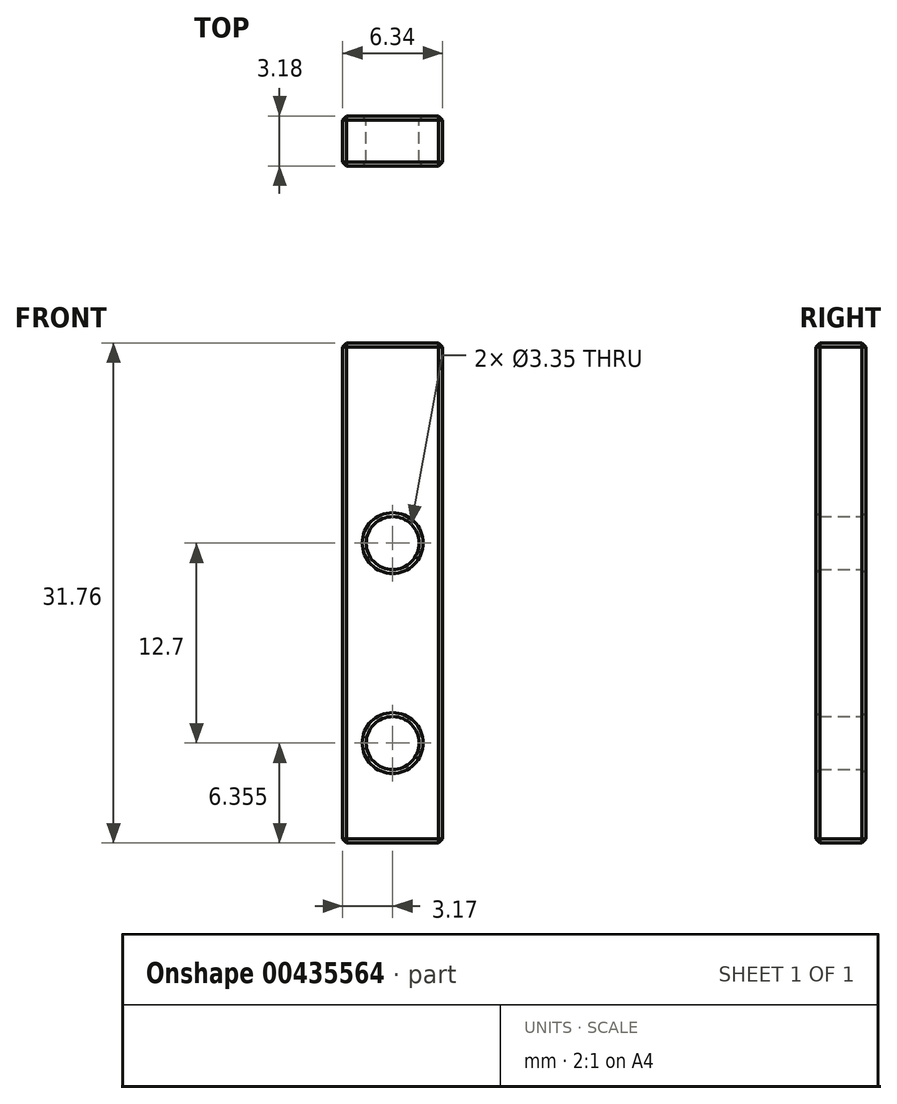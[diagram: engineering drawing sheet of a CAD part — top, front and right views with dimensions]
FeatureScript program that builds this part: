
annotation { "Feature Type Name" : "Feature", "Feature Type Description" : "" }
export const myFeature = defineFeature(function(context is Context, id is Id, definition is map)
    precondition{}
    {
        {
            var Q0;
            Q0=qCreatedBy(makeId("Front.planeOp"),FACE);
            var sketch = newSketch(context, id + "F0", { "sketchPlane" : qUnion([Q0])});
            skLineSegment(sketch, "E0.bottom", {"start": v(-3.18, -15.88) * mm, "end": v(3.17, -15.88) * mm});
            skLineSegment(sketch, "E0.top", {"start": v(-3.17, 15.88) * mm, "end": v(3.18, 15.88) * mm});
            skLineSegment(sketch, "E0.left", {"start": v(-3.18, -15.88) * mm, "end": v(-3.17, 15.88) * mm});
            skLineSegment(sketch, "E0.right", {"start": v(3.17, -15.88) * mm, "end": v(3.18, 15.88) * mm});
            skPoint(sketch, "E0.middle", {"position": v(0, 0) * mm});
            skCircle(sketch, "E1", {"center": v(0, 3.18) * mm, "radius": 1.68 * mm});
            skCircle(sketch, "E2", {"center": v(0, -9.52) * mm, "radius": 1.68 * mm});
            skSolve(sketch);
        }
        {
            var Q0;
            Q0=makeQuery(id+"F0.imprint","IMPRINT",FACE,{"disambiguationData":[TD([[makeQuery(id+"F0.imprint","IMPRINT",EDGE,{"derivedFrom":sQuery(id+"F0.wireOp",EDGE,"E0.bottom")}),1.0]])]});
            extrude(context, id + "F1", {"entities" : qUnion([Q0]), "depth" : 3.17 * mm});
        }
        {
            var Q0;
            Q0=makeQuery(id+"F1.opExtrude","CAP_EDGE",EDGE,{"disambiguationData":[OSD([sQuery(id+"F0.wireOp",EDGE,"E1")])],"isStart":false});
            var Q1;
            Q1=makeQuery(id+"F1.opExtrude","CAP_EDGE",EDGE,{"disambiguationData":[OSD([sQuery(id+"F0.wireOp",EDGE,"E2")])],"isStart":false});
            var Q2;
            Q2=makeQuery(id+"F1.opExtrude","SWEPT_EDGE",EDGE,{"disambiguationData":[OSD([sQuery(id+"F0.wireOp",EDGE,"E0.bottom"),sQuery(id+"F0.wireOp",EDGE,"E0.right")])]});
            var Q3;
            Q3=makeQuery(id+"F1.opExtrude","SWEPT_EDGE",EDGE,{"disambiguationData":[OSD([sQuery(id+"F0.wireOp",EDGE,"E0.top"),sQuery(id+"F0.wireOp",EDGE,"E0.left")])]});
            var Q4;
            Q4=makeQuery(id+"F1.opExtrude","SWEPT_EDGE",EDGE,{"disambiguationData":[OSD([sQuery(id+"F0.wireOp",EDGE,"E0.top"),sQuery(id+"F0.wireOp",EDGE,"E0.right")])]});
            var Q5;
            Q5=makeQuery(id+"F1.opExtrude","CAP_EDGE",EDGE,{"disambiguationData":[OSD([sQuery(id+"F0.wireOp",EDGE,"E2")])],"isStart":true});
            var Q6;
            Q6=makeQuery(id+"F1.opExtrude","SWEPT_EDGE",EDGE,{"disambiguationData":[OSD([sQuery(id+"F0.wireOp",EDGE,"E0.bottom"),sQuery(id+"F0.wireOp",EDGE,"E0.left")])]});
            var Q7;
            Q7=makeQuery(id+"F1.opExtrude","CAP_EDGE",EDGE,{"disambiguationData":[OSD([sQuery(id+"F0.wireOp",EDGE,"E0.bottom")])],"isStart":true});
            var Q8;
            Q8=makeQuery(id+"F1.opExtrude","CAP_EDGE",EDGE,{"disambiguationData":[OSD([sQuery(id+"F0.wireOp",EDGE,"E0.bottom")])],"isStart":false});
            var Q9;
            Q9=makeQuery(id+"F1.opExtrude","CAP_EDGE",EDGE,{"disambiguationData":[OSD([sQuery(id+"F0.wireOp",EDGE,"E0.top")])],"isStart":true});
            var Q10;
            Q10=makeQuery(id+"F1.opExtrude","CAP_EDGE",EDGE,{"disambiguationData":[OSD([sQuery(id+"F0.wireOp",EDGE,"E0.top")])],"isStart":false});
            var Q11;
            Q11=makeQuery(id+"F1.opExtrude","CAP_EDGE",EDGE,{"disambiguationData":[OSD([sQuery(id+"F0.wireOp",EDGE,"E0.left")])],"isStart":true});
            var Q12;
            Q12=makeQuery(id+"F1.opExtrude","CAP_EDGE",EDGE,{"disambiguationData":[OSD([sQuery(id+"F0.wireOp",EDGE,"E0.left")])],"isStart":false});
            var Q13;
            Q13=makeQuery(id+"F1.opExtrude","CAP_EDGE",EDGE,{"disambiguationData":[OSD([sQuery(id+"F0.wireOp",EDGE,"E0.right")])],"isStart":true});
            var Q14;
            Q14=makeQuery(id+"F1.opExtrude","CAP_EDGE",EDGE,{"disambiguationData":[OSD([sQuery(id+"F0.wireOp",EDGE,"E0.right")])],"isStart":false});
            var Q15;
            Q15=makeQuery(id+"F1.opExtrude","CAP_EDGE",EDGE,{"disambiguationData":[OSD([sQuery(id+"F0.wireOp",EDGE,"E1")])],"isStart":true});
            chamfer(context, id + "F2", {"entities" : qUnion([Q0, Q1, Q2, Q3, Q4, Q5, Q6, Q7, Q8, Q9, Q10, Q11, Q12, Q13, Q14, Q15]), "width" : 0.25 * mm, "tangentPropagation" : true});
        }
    });
